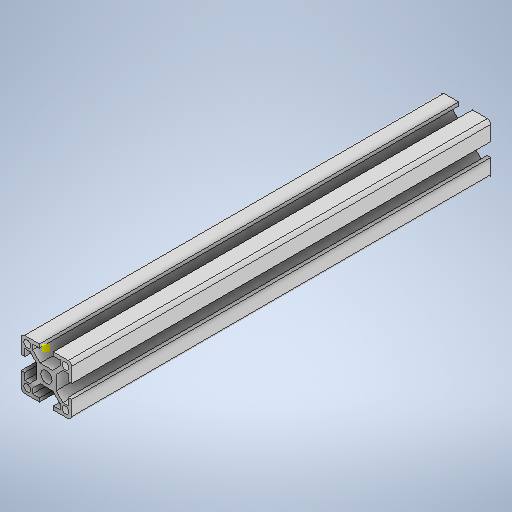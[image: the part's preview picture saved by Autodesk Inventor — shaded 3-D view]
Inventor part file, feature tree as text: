
AUTODESK INVENTOR PART (.ipt)
format: ipt  version: 2025 (Build 290162000, 162)  size: 307,200 bytes
history: native  units: in
note: dims shown in document units (in); Inventor stores cm internally (conversion verified against a paired STEP export)
features: sketch x2, extrude x1
ambient origin geometry x8: Origin, YZ Plane, XZ Plane, XY Plane, X Axis, Y Axis, Z Axis, Center Point
bodies: Solid1 (feature_tree)
feature tree (3):
  extrude  "Extrusion1"  Depth=9.8425in
  sketch  "Sketch2"  dims[d9=0.0344in]
  sketch  "Sketch1"  dims[d6=9.8425in d7=0.0in d8=0.1969in]
